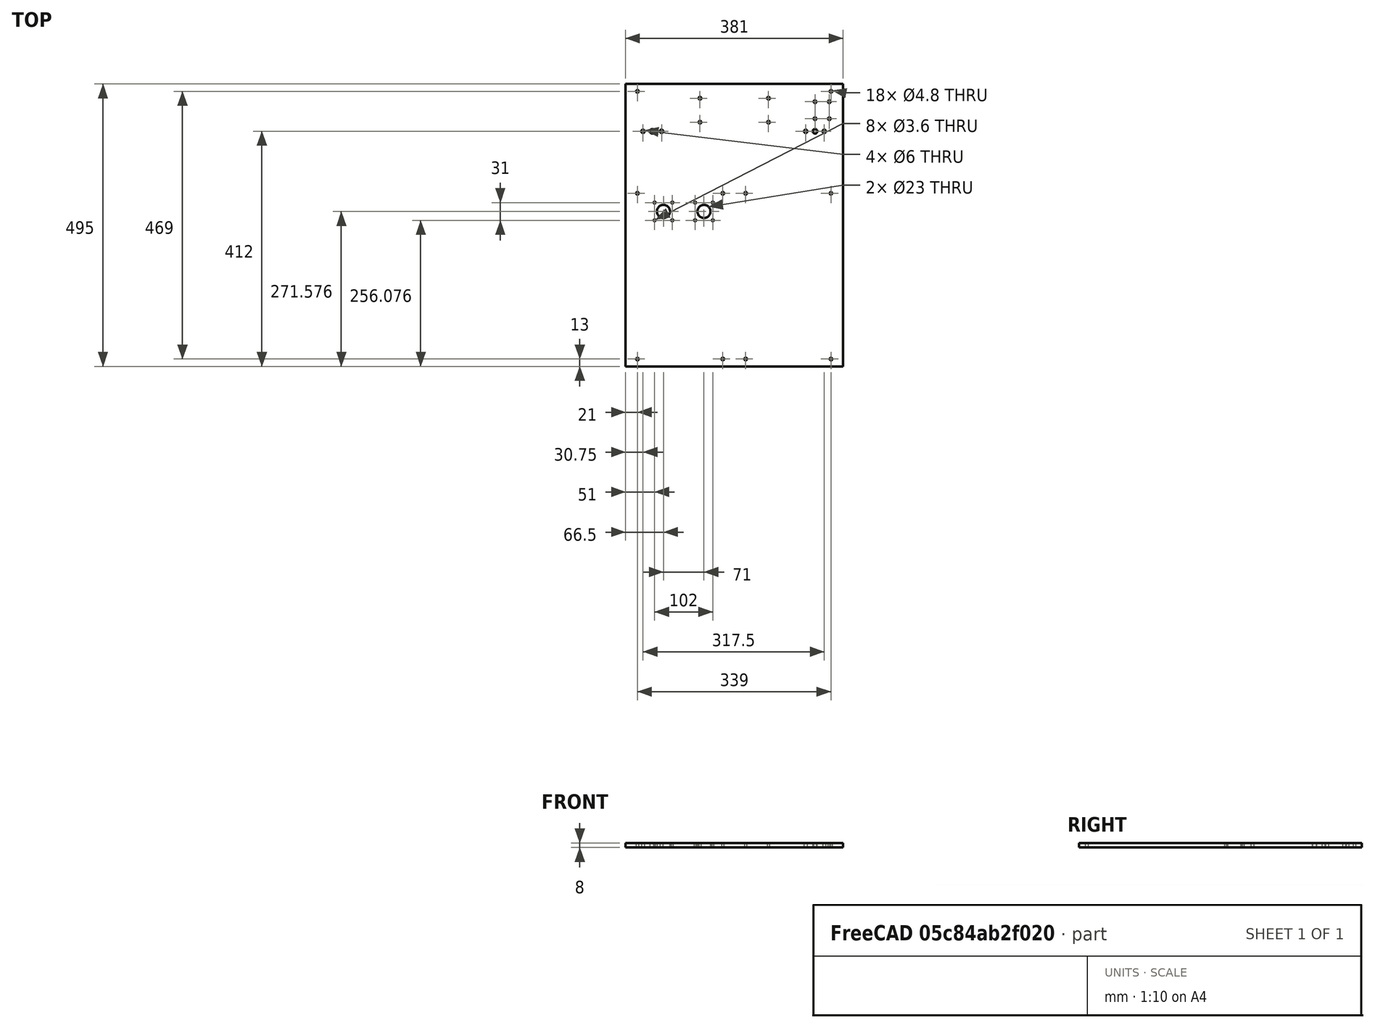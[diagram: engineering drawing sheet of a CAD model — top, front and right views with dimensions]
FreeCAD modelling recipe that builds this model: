
FCSTD DOCUMENT  (FreeCAD 0.16R6706 (Git))
Label: Fundo
License: All rights reserved
LicenseURL: http://en.wikipedia.org/wiki/All_rights_reserved
objects: Path::FeaturePython×37, Sketcher::SketchObject×1, PartDesign::Pad×1, Path::FeatureCompoundPython×1
note: 3 computed .brp shape members not serialized (recipe doc carries the construction recipe); baked Part::Feature solids carry a one-line shape summary decoded from their .brp

FEATURE [Sketcher::SketchObject] Sketch
  sketch-geometry (63):
    g0: LineSegment StartX=-381 StartY=495 StartZ=0 EndX=0 EndY=495 EndZ=0
    g1: LineSegment StartX=0 StartY=495 StartZ=0 EndX=0 EndY=0 EndZ=0
    g2: LineSegment StartX=-381 StartY=0 StartZ=0 EndX=-381 EndY=495 EndZ=0
    g3: LineSegment [constr] StartX=-334 StartY=400 StartZ=0 EndX=-334 EndY=412 EndZ=0
    g4: LineSegment [constr] StartX=-350.25 StartY=412 StartZ=0 EndX=-317.75 EndY=412 EndZ=0
    g5: Circle CenterX=-350.25 CenterY=412 CenterZ=0 NormalX=0 NormalY=0 NormalZ=1 Radius=3
    g6: Circle CenterX=-317.75 CenterY=412 CenterZ=0 NormalX=0 NormalY=0 NormalZ=1 Radius=3
    g7: Circle CenterX=-334 CenterY=412 CenterZ=0 NormalX=0 NormalY=0 NormalZ=1 Radius=4.05
    g8: LineSegment [constr] StartX=-334 StartY=412 StartZ=0 EndX=-49 EndY=412 EndZ=0
    g9: LineSegment [constr] StartX=-65.25 StartY=412 StartZ=0 EndX=-32.75 EndY=412 EndZ=0
    g10: Circle CenterX=-65.25 CenterY=412 CenterZ=0 NormalX=0 NormalY=0 NormalZ=1 Radius=3
    g11: Circle CenterX=-32.75 CenterY=412 CenterZ=0 NormalX=0 NormalY=0 NormalZ=1 Radius=3
    g12: Circle CenterX=-49 CenterY=412 CenterZ=0 NormalX=0 NormalY=0 NormalZ=1 Radius=4.05
    g13: LineSegment StartX=0 StartY=0 StartZ=0 EndX=-381 EndY=0 EndZ=0
    g14: Circle CenterX=-21 CenterY=482 CenterZ=0 NormalX=0 NormalY=0 NormalZ=1 Radius=2.4
    g15: LineSegment [constr] StartX=-360 StartY=482 StartZ=0 EndX=-21 EndY=482 EndZ=0
    g16: LineSegment [constr] StartX=-21 StartY=482 StartZ=0 EndX=-21 EndY=13 EndZ=0
    g17: LineSegment [constr] StartX=-21 StartY=13 StartZ=0 EndX=-360 EndY=13 EndZ=0
    g18: LineSegment [constr] StartX=-360 StartY=13 StartZ=0 EndX=-360 EndY=482 EndZ=0
    g19: Circle CenterX=-360 CenterY=482 CenterZ=0 NormalX=0 NormalY=0 NormalZ=1 Radius=2.4
    g20: Circle CenterX=-21 CenterY=13 CenterZ=0 NormalX=0 NormalY=0 NormalZ=1 Radius=2.4
    g21: Circle CenterX=-360 CenterY=13 CenterZ=0 NormalX=0 NormalY=0 NormalZ=1 Radius=2.4
    g22: LineSegment [constr] StartX=-250.5 StartY=470 StartZ=0 EndX=-250.5 EndY=428 EndZ=0
    g23: Circle CenterX=-250.5 CenterY=470 CenterZ=0 NormalX=0 NormalY=0 NormalZ=1 Radius=2.4
    g24: Circle CenterX=-250.5 CenterY=428 CenterZ=0 NormalX=0 NormalY=0 NormalZ=1 Radius=2.4
    g25: LineSegment [constr] StartX=-250.5 StartY=449 StartZ=0 EndX=-56.1898 EndY=449 EndZ=0
    g26: LineSegment [constr] StartX=-190.5 StartY=452.155 StartZ=0 EndX=-190.5 EndY=169.463 EndZ=0
    g27: LineSegment [constr] StartX=-210.5 StartY=303.4 StartZ=0 EndX=-170.5 EndY=303.4 EndZ=0
    g28: Circle CenterX=-210.5 CenterY=303.4 CenterZ=0 NormalX=0 NormalY=0 NormalZ=1 Radius=2.4
    g29: Circle CenterX=-170.5 CenterY=303.4 CenterZ=0 NormalX=0 NormalY=0 NormalZ=1 Radius=2.4
    g30: Circle CenterX=-360 CenterY=303.4 CenterZ=0 NormalX=0 NormalY=0 NormalZ=1 Radius=2.4
    g31: Circle CenterX=-21 CenterY=303.4 CenterZ=0 NormalX=0 NormalY=0 NormalZ=1 Radius=2.4
    g32: LineSegment [constr] StartX=-49 StartY=463.9 StartZ=0 EndX=-24 EndY=463.9 EndZ=0
    g33: LineSegment [constr] StartX=-24 StartY=463.9 StartZ=0 EndX=-24 EndY=434.1 EndZ=0
    g34: LineSegment [constr] StartX=-24 StartY=434.1 StartZ=0 EndX=-49 EndY=434.1 EndZ=0
    g35: LineSegment [constr] StartX=-49 StartY=434.1 StartZ=0 EndX=-49 EndY=463.9 EndZ=0
    g36: Circle CenterX=-49 CenterY=463.9 CenterZ=0 NormalX=0 NormalY=0 NormalZ=1 Radius=2.4
    g37: Circle CenterX=-24 CenterY=463.9 CenterZ=0 NormalX=0 NormalY=0 NormalZ=1 Radius=2.4
    g38: Circle CenterX=-24 CenterY=434.1 CenterZ=0 NormalX=0 NormalY=0 NormalZ=1 Radius=2.4
    g39: Circle CenterX=-49 CenterY=434.1 CenterZ=0 NormalX=0 NormalY=0 NormalZ=1 Radius=2.4
    g40: Circle CenterX=-210.5 CenterY=13 CenterZ=0 NormalX=0 NormalY=0 NormalZ=1 Radius=2.4
    g41: Circle CenterX=-170.5 CenterY=13 CenterZ=0 NormalX=0 NormalY=0 NormalZ=1 Radius=2.4
    g42: LineSegment [constr] StartX=-330 StartY=287.076 StartZ=0 EndX=-299 EndY=287.076 EndZ=0
    g43: LineSegment [constr] StartX=-299 StartY=287.076 StartZ=0 EndX=-299 EndY=256.076 EndZ=0
    g44: LineSegment [constr] StartX=-299 StartY=256.076 StartZ=0 EndX=-330 EndY=256.076 EndZ=0
    g45: LineSegment [constr] StartX=-330 StartY=256.076 StartZ=0 EndX=-330 EndY=287.076 EndZ=0
    g46: Circle CenterX=-314.5 CenterY=271.576 CenterZ=0 NormalX=0 NormalY=0 NormalZ=1 Radius=11.5
    g47: Circle CenterX=-330 CenterY=287.076 CenterZ=0 NormalX=0 NormalY=0 NormalZ=1 Radius=1.8
    g48: Circle CenterX=-299 CenterY=287.076 CenterZ=0 NormalX=0 NormalY=0 NormalZ=1 Radius=1.8
    g49: Circle CenterX=-299 CenterY=256.076 CenterZ=0 NormalX=0 NormalY=0 NormalZ=1 Radius=1.8
    g50: Circle CenterX=-330 CenterY=256.076 CenterZ=0 NormalX=0 NormalY=0 NormalZ=1 Radius=1.8
    g51: LineSegment [constr] StartX=-259 StartY=287.076 StartZ=0 EndX=-228 EndY=287.076 EndZ=0
    g52: LineSegment [constr] StartX=-228 StartY=287.076 StartZ=0 EndX=-228 EndY=256.076 EndZ=0
    g53: LineSegment [constr] StartX=-228 StartY=256.076 StartZ=0 EndX=-259 EndY=256.076 EndZ=0
    g54: LineSegment [constr] StartX=-259 StartY=256.076 StartZ=0 EndX=-259 EndY=287.076 EndZ=0
    g55: Circle CenterX=-243.5 CenterY=271.576 CenterZ=0 NormalX=0 NormalY=0 NormalZ=1 Radius=11.5
    g56: Circle CenterX=-259 CenterY=287.076 CenterZ=0 NormalX=0 NormalY=0 NormalZ=1 Radius=1.8
    g57: Circle CenterX=-228 CenterY=287.076 CenterZ=0 NormalX=0 NormalY=0 NormalZ=1 Radius=1.8
    g58: Circle CenterX=-228 CenterY=256.076 CenterZ=0 NormalX=0 NormalY=0 NormalZ=1 Radius=1.8
    g59: Circle CenterX=-259 CenterY=256.076 CenterZ=0 NormalX=0 NormalY=0 NormalZ=1 Radius=1.8
    g60: LineSegment [constr] StartX=-130.5 StartY=470 StartZ=0 EndX=-130.5 EndY=428 EndZ=0
    g61: Circle CenterX=-130.5 CenterY=470 CenterZ=0 NormalX=0 NormalY=0 NormalZ=1 Radius=2.4
    g62: Circle CenterX=-130.5 CenterY=428 CenterZ=0 NormalX=0 NormalY=0 NormalZ=1 Radius=2.4
  constraints (159):
    c: Coincident(g0,g1)
    c: Coincident(g2,g0)
    c: Horizontal(g0)
    c: Vertical(g1)
    c: Vertical(g2)
    c: DistanceY(g1,g1) = 495
    c: Vertical(g3)
    c: Horizontal(g4)
    c: DistanceX(g4,g4) = 32.5
    c: Radius(g5) = 3
    c: Equal(g5,g6) = 3
    c: Coincident(g4,g6)
    c: Coincident(g5,g4)
    c: Radius(g7) = 4.05
    c: Symmetric(g4,g4,g7)
    c: Coincident(g3,g7)
    c: Horizontal(g8)
    c: DistanceX(g8,g8) = 285
    c: Coincident(g3,g8)
    c: Horizontal(g9)
    c: Equal(g4,g9) = 32.5
    c: Equal(g5,g10) = 3
    c: Equal(g10,g11) = 3
    c: Coincident(g9,g11)
    c: Coincident(g10,g9)
    c: Equal(g7,g12) = 4.2
    c: Symmetric(g9,g9,g12)
    c: Coincident(g2,g13)
    c: Coincident(g1,g13)
    c: Horizontal(g13)
    c: Coincident(g12,g8)
    c: PointOnObject(g2,g-1)
    c: Coincident(g1,g-1)
    c: Radius(g14) = 2.4
    c: Coincident(g15,g16)
    c: Coincident(g16,g17)
    c: Coincident(g17,g18)
    c: Coincident(g18,g15)
    c: Horizontal(g15)
    c: Horizontal(g17)
    c: Vertical(g16)
    c: Vertical(g18)
    c: Coincident(g15,g14)
    c: DistanceX(g14,g0) = 21
    c: DistanceX(g15,g15) = 339
    c: DistanceX(g13,g13) = 381
    c: Equal(g14,g19) = 2.25
    c: Coincident(g15,g19)
    c: DistanceY(g14,g0) = 13
    c: DistanceX(g0,g15) = 21
    c: DistanceX(g8,g0) = 49
    c: DistanceX(g0,g3) = 47
    c: DistanceY(g2,g17) = 13
    c: Equal(g14,g20) = 2.25
    c: Equal(g14,g21) = 2.25
    c: Coincident(g17,g21)
    c: Coincident(g16,g20)
    c: Vertical(g22)
    c: Coincident(g22,g23)
    c: Coincident(g22,g24)
    c: DistanceY(g25,g14) = 33
    c: DistanceY(g22,g22) = 42
    c: Symmetric(g22,g22,g25)
    c: DistanceY(g8,g25) = 37
    c: Symmetric(g0,g0,g26)
    c: DistanceX(g25,g26) = 60
    c: Radius(g23) = 2.4
    c: Equal(g23,g24)
    c: Horizontal(g27)
    c: DistanceX(g27,g27) = 40
    c: Symmetric(g27,g27,g26)
    c: DistanceY(g27,g0) = 191.6
    c: Radius(g28) = 2.4
    c: Equal(g28,g29) = 2.4
    c: Coincident(g27,g29)
    c: Coincident(g27,g28)
    c: Equal(g28,g30) = 2.4
    c: Equal(g28,g31) = 2.4
    c: PointOnObject(g31,g27)
    c: PointOnObject(g30,g27)
    c: PointOnObject(g30,g18)
    c: PointOnObject(g31,g16)
    c: Coincident(g32,g33)
    c: Coincident(g33,g34)
    c: Coincident(g34,g35)
    c: Coincident(g35,g32)
    c: Horizontal(g32)
    c: Horizontal(g34)
    c: Vertical(g33)
    c: Vertical(g35)
    c: DistanceY(g35,g35) = 29.8
    c: DistanceX(g32,g32) = 25
    c: Symmetric(g32,g34,g25)
    c: DistanceX(g32,g0) = 49
    c: Radius(g36) = 2.4
    c: Equal(g36,g37) = 2.4
    c: Equal(g36,g38) = 2.4
    c: Equal(g36,g39) = 2.4
    c: Coincident(g32,g36)
    c: Coincident(g32,g37)
    c: Coincident(g33,g38)
    c: Coincident(g34,g39)
    c: Radius(g40) = 2.4
    c: Equal(g40,g41) = 2.4
    c: DistanceX(g40,g41) = 40
    c: PointOnObject(g40,g17)
    c: PointOnObject(g41,g17)
    c: DistanceX(g17,g40) = 149.5
    c: Coincident(g42,g43)
    c: Coincident(g43,g44)
    c: Coincident(g44,g45)
    c: Coincident(g45,g42)
    c: Horizontal(g42)
    c: Horizontal(g44)
    c: Vertical(g43)
    c: Vertical(g45)
    c: DistanceX(g42,g42) = 31
    c: Equal(g42,g45)
    c: Radius(g46) = 11.5
    c: Symmetric(g42,g44,g46)
    c: Radius(g47) = 1.8
    c: Equal(g47,g48) = 1.8
    c: Equal(g47,g49) = 1.8
    c: Equal(g47,g50) = 1.8
    c: Coincident(g47,g42)
    c: Coincident(g48,g42)
    c: Coincident(g43,g49)
    c: Coincident(g44,g50)
    c: Coincident(g51,g52)
    c: Coincident(g52,g53)
    c: Coincident(g53,g54)
    c: Coincident(g54,g51)
    c: Horizontal(g51)
    c: Horizontal(g53)
    c: Vertical(g52)
    c: Vertical(g54)
    c: Equal(g42,g51) = 31
    c: Equal(g51,g54)
    c: Equal(g46,g55) = 11.5
    c: Symmetric(g51,g53,g55)
    c: Equal(g47,g56) = 1.8
    c: Equal(g56,g57) = 1.8
    c: Equal(g56,g58) = 1.8
    c: Equal(g56,g59) = 1.8
    c: Coincident(g56,g51)
    c: Coincident(g57,g51)
    c: Coincident(g52,g58)
    c: Coincident(g53,g59)
    c: PointOnObject(g51,g42)
    c: DistanceX(g42,g51) = 40
    c: DistanceX(g30,g42) = 30
    c: Equal(g22,g60)
    c: Vertical(g60)
    c: Symmetric(g60,g60,g25)
    c: Equal(g23,g61) = 2.4
    c: Equal(g23,g62) = 2.4
    c: Coincident(g60,g62)
    c: Coincident(g61,g60)
    c: DistanceX(g26,g60) = 60
FEATURE [PartDesign::Pad] Pad
  Length = 8
  Length2 = 100
  Sketch = -> Sketch
  Type = 0
FEATURE [Path::FeaturePython] Machine  label="Machine_"  # Path/CAM operation (typed FeaturePython)
  MachineUnits = 0
  X = 0
  X_Max = 0
  X_Min = 0
  Y = 0
  Y_Max = 0
  Y_Min = 0
  Z = 0
  Z_Max = 0
  Z_Min = 0
FEATURE [Path::FeaturePython] Tool  label="Tool1"  # Path/CAM operation (typed FeaturePython)
  SpindleDir = 0
  SpindleSpeed = 0
  ToolNumber = 1
FEATURE [Path::FeaturePython] Profile  label="Cantoneiras"  # Path/CAM operation (typed FeaturePython)
  Active = true
  Base = -> Pad
  ClearanceHeight = 3.1
  Direction = 1
  Edge1 = -> Pad [Edge39]
  EndPoint = (0,0,0)
  ExtendAtEnd = 0
  ExtendAtStart = 0
  FinalDepth = -8.15
  HorizFeed = 127
  LeadInLineLen = 0
  LeadOutLineLen = 0
  OffsetExtra = 0
  PathClosed = true
  RetractHeight = 0
  RollRadius = 0
  SegLen = 0.5
  Side = 1
  StartDepth = 0
  StartPoint = (0,0,0)
  StepDown = 3
  ToolNumber = 1
  UseEndPoint = false
  UsePlacements = false
  UseStartDepth = true
  UseStartPoint = false
  VertFeed = 127
FEATURE [Path::FeaturePython] Profile001  label="Cantoneiras001"  # Path/CAM operation (typed FeaturePython)
  Active = true
  Base = -> Pad
  ClearanceHeight = 3.1
  Direction = 1
  Edge1 = -> Pad [Edge51]
  EndPoint = (0,0,0)
  ExtendAtEnd = 0
  ExtendAtStart = 0
  FinalDepth = -8.15
  HorizFeed = 127
  LeadInLineLen = 0
  LeadOutLineLen = 0
  OffsetExtra = 0
  PathClosed = true
  RetractHeight = 0
  RollRadius = 0
  SegLen = 0.5
  Side = 1
  StartDepth = 0
  StartPoint = (0,0,0)
  StepDown = 3
  ToolNumber = 1
  UseEndPoint = false
  UsePlacements = false
  UseStartDepth = true
  UseStartPoint = false
  VertFeed = 127
FEATURE [Path::FeaturePython] Profile002  label="Cantoneiras002"  # Path/CAM operation (typed FeaturePython)
  Active = true
  Base = -> Pad
  ClearanceHeight = 3.1
  Direction = 1
  Edge1 = -> Pad [Edge48]
  EndPoint = (0,0,0)
  ExtendAtEnd = 0
  ExtendAtStart = 0
  FinalDepth = -8.15
  HorizFeed = 127
  LeadInLineLen = 0
  LeadOutLineLen = 0
  OffsetExtra = 0
  PathClosed = true
  RetractHeight = 0
  RollRadius = 0
  SegLen = 0.5
  Side = 1
  StartDepth = 0
  StartPoint = (0,0,0)
  StepDown = 3
  ToolNumber = 1
  UseEndPoint = false
  UsePlacements = false
  UseStartDepth = true
  UseStartPoint = false
  VertFeed = 127
FEATURE [Path::FeaturePython] Profile003  label="Cantoneiras003"  # Path/CAM operation (typed FeaturePython)
  Active = true
  Base = -> Pad
  ClearanceHeight = 3.1
  Direction = 1
  Edge1 = -> Pad [Edge69]
  EndPoint = (0,0,0)
  ExtendAtEnd = 0
  ExtendAtStart = 0
  FinalDepth = -8.15
  HorizFeed = 127
  LeadInLineLen = 0
  LeadOutLineLen = 0
  OffsetExtra = 0
  PathClosed = true
  RetractHeight = 0
  RollRadius = 0
  SegLen = 0.5
  Side = 1
  StartDepth = 0
  StartPoint = (0,0,0)
  StepDown = 3
  ToolNumber = 1
  UseEndPoint = false
  UsePlacements = false
  UseStartDepth = true
  UseStartPoint = false
  VertFeed = 127
FEATURE [Path::FeaturePython] Profile004  label="Cantoneiras004"  # Path/CAM operation (typed FeaturePython)
  Active = true
  Base = -> Pad
  ClearanceHeight = 3.1
  Direction = 1
  Edge1 = -> Pad [Edge72]
  EndPoint = (0,0,0)
  ExtendAtEnd = 0
  ExtendAtStart = 0
  FinalDepth = -8.15
  HorizFeed = 127
  LeadInLineLen = 0
  LeadOutLineLen = 0
  OffsetExtra = 0
  PathClosed = true
  RetractHeight = 0
  RollRadius = 0
  SegLen = 0.5
  Side = 1
  StartDepth = 0
  StartPoint = (0,0,0)
  StepDown = 3
  ToolNumber = 1
  UseEndPoint = false
  UsePlacements = false
  UseStartDepth = true
  UseStartPoint = false
  VertFeed = 127
FEATURE [Path::FeaturePython] Profile005  label="Cantoneiras005"  # Path/CAM operation (typed FeaturePython)
  Active = true
  Base = -> Pad
  ClearanceHeight = 3.1
  Direction = 1
  Edge1 = -> Pad [Edge42]
  EndPoint = (0,0,0)
  ExtendAtEnd = 0
  ExtendAtStart = 0
  FinalDepth = -8.15
  HorizFeed = 127
  LeadInLineLen = 0
  LeadOutLineLen = 0
  OffsetExtra = 0
  PathClosed = true
  RetractHeight = 0
  RollRadius = 0
  SegLen = 0.5
  Side = 1
  StartDepth = 0
  StartPoint = (0,0,0)
  StepDown = 3
  ToolNumber = 1
  UseEndPoint = false
  UsePlacements = false
  UseStartDepth = true
  UseStartPoint = false
  VertFeed = 127
FEATURE [Path::FeaturePython] Profile006  label="Cantoneiras006"  # Path/CAM operation (typed FeaturePython)
  Active = true
  Base = -> Pad
  ClearanceHeight = 3.1
  Direction = 1
  Edge1 = -> Pad [Edge63]
  EndPoint = (0,0,0)
  ExtendAtEnd = 0
  ExtendAtStart = 0
  FinalDepth = -8.15
  HorizFeed = 127
  LeadInLineLen = 0
  LeadOutLineLen = 0
  OffsetExtra = 0
  PathClosed = true
  RetractHeight = 0
  RollRadius = 0
  SegLen = 0.5
  Side = 1
  StartDepth = 0
  StartPoint = (0,0,0)
  StepDown = 3
  ToolNumber = 1
  UseEndPoint = false
  UsePlacements = false
  UseStartDepth = true
  UseStartPoint = false
  VertFeed = 127
FEATURE [Path::FeaturePython] Profile007  label="Cantoneiras007"  # Path/CAM operation (typed FeaturePython)
  Active = true
  Base = -> Pad
  ClearanceHeight = 3.1
  Direction = 1
  Edge1 = -> Pad [Edge90]
  EndPoint = (0,0,0)
  ExtendAtEnd = 0
  ExtendAtStart = 0
  FinalDepth = -8.15
  HorizFeed = 127
  LeadInLineLen = 0
  LeadOutLineLen = 0
  OffsetExtra = 0
  PathClosed = true
  RetractHeight = 0
  RollRadius = 0
  SegLen = 0.5
  Side = 1
  StartDepth = 0
  StartPoint = (0,0,0)
  StepDown = 3
  ToolNumber = 1
  UseEndPoint = false
  UsePlacements = false
  UseStartDepth = true
  UseStartPoint = false
  VertFeed = 127
FEATURE [Path::FeaturePython] Profile008  label="Cantoneiras008"  # Path/CAM operation (typed FeaturePython)
  Active = true
  Base = -> Pad
  ClearanceHeight = 3.1
  Direction = 1
  Edge1 = -> Pad [Edge87]
  EndPoint = (0,0,0)
  ExtendAtEnd = 0
  ExtendAtStart = 0
  FinalDepth = -8.15
  HorizFeed = 127
  LeadInLineLen = 0
  LeadOutLineLen = 0
  OffsetExtra = 0
  PathClosed = true
  RetractHeight = 0
  RollRadius = 0
  SegLen = 0.5
  Side = 1
  StartDepth = 0
  StartPoint = (0,0,0)
  StepDown = 3
  ToolNumber = 1
  UseEndPoint = false
  UsePlacements = false
  UseStartDepth = true
  UseStartPoint = false
  VertFeed = 127
FEATURE [Path::FeaturePython] Profile009  label="Cantoneiras009"  # Path/CAM operation (typed FeaturePython)
  Active = true
  Base = -> Pad
  ClearanceHeight = 3.1
  Direction = 1
  Edge1 = -> Pad [Edge84]
  EndPoint = (0,0,0)
  ExtendAtEnd = 0
  ExtendAtStart = 0
  FinalDepth = -8.15
  HorizFeed = 127
  LeadInLineLen = 0
  LeadOutLineLen = 0
  OffsetExtra = 0
  PathClosed = true
  RetractHeight = 0
  RollRadius = 0
  SegLen = 0.5
  Side = 1
  StartDepth = 0
  StartPoint = (0,0,0)
  StepDown = 3
  ToolNumber = 1
  UseEndPoint = false
  UsePlacements = false
  UseStartDepth = true
  UseStartPoint = false
  VertFeed = 127
FEATURE [Path::FeaturePython] Profile010  label="Motores"  # Path/CAM operation (typed FeaturePython)
  Active = true
  Base = -> Pad
  ClearanceHeight = 3.1
  Direction = 1
  Edge1 = -> Pad [Edge93]
  EndPoint = (0,0,0)
  ExtendAtEnd = 0
  ExtendAtStart = 0
  FinalDepth = -8.15
  HorizFeed = 127
  LeadInLineLen = 0
  LeadOutLineLen = 0
  OffsetExtra = 0
  PathClosed = true
  RetractHeight = 0
  RollRadius = 0
  SegLen = 0.5
  Side = 1
  StartDepth = 0
  StartPoint = (0,0,0)
  StepDown = 3
  ToolNumber = 1
  UseEndPoint = false
  UsePlacements = false
  UseStartDepth = true
  UseStartPoint = false
  VertFeed = 127
FEATURE [Path::FeaturePython] Profile011  label="Motores001"  # Path/CAM operation (typed FeaturePython)
  Active = true
  Base = -> Pad
  ClearanceHeight = 3.1
  Direction = 1
  Edge1 = -> Pad [Edge96]
  EndPoint = (0,0,0)
  ExtendAtEnd = 0
  ExtendAtStart = 0
  FinalDepth = -8.15
  HorizFeed = 127
  LeadInLineLen = 0
  LeadOutLineLen = 0
  OffsetExtra = 0
  PathClosed = true
  RetractHeight = 0
  RollRadius = 0
  SegLen = 0.5
  Side = 1
  StartDepth = 0
  StartPoint = (0,0,0)
  StepDown = 3
  ToolNumber = 1
  UseEndPoint = false
  UsePlacements = false
  UseStartDepth = true
  UseStartPoint = false
  VertFeed = 127
FEATURE [Path::FeaturePython] Profile012  label="Motores002"  # Path/CAM operation (typed FeaturePython)
  Active = true
  Base = -> Pad
  ClearanceHeight = 3.1
  Direction = 1
  Edge1 = -> Pad [Edge18]
  EndPoint = (0,0,0)
  ExtendAtEnd = 0
  ExtendAtStart = 0
  FinalDepth = -8.15
  HorizFeed = 127
  LeadInLineLen = 0
  LeadOutLineLen = 0
  OffsetExtra = 0
  PathClosed = true
  RetractHeight = 0
  RollRadius = 0
  SegLen = 0.5
  Side = 1
  StartDepth = 0
  StartPoint = (0,0,0)
  StepDown = 3
  ToolNumber = 1
  UseEndPoint = false
  UsePlacements = false
  UseStartDepth = true
  UseStartPoint = false
  VertFeed = 127
FEATURE [Path::FeaturePython] Profile013  label="Motores003"  # Path/CAM operation (typed FeaturePython)
  Active = true
  Base = -> Pad
  ClearanceHeight = 3.1
  Direction = 1
  Edge1 = -> Pad [Edge114]
  EndPoint = (0,0,0)
  ExtendAtEnd = 0
  ExtendAtStart = 0
  FinalDepth = -8.15
  HorizFeed = 127
  LeadInLineLen = 0
  LeadOutLineLen = 0
  OffsetExtra = 0
  PathClosed = true
  RetractHeight = 0
  RollRadius = 0
  SegLen = 0.5
  Side = 1
  StartDepth = 0
  StartPoint = (0,0,0)
  StepDown = 3
  ToolNumber = 1
  UseEndPoint = false
  UsePlacements = false
  UseStartDepth = true
  UseStartPoint = false
  VertFeed = 127
FEATURE [Path::FeaturePython] Profile014  label="Motores004"  # Path/CAM operation (typed FeaturePython)
  Active = true
  Base = -> Pad
  ClearanceHeight = 3.1
  Direction = 1
  Edge1 = -> Pad [Edge99]
  EndPoint = (0,0,0)
  ExtendAtEnd = 0
  ExtendAtStart = 0
  FinalDepth = -8.15
  HorizFeed = 127
  LeadInLineLen = 0
  LeadOutLineLen = 0
  OffsetExtra = 0
  PathClosed = true
  RetractHeight = 0
  RollRadius = 0
  SegLen = 0.5
  Side = 1
  StartDepth = 0
  StartPoint = (0,0,0)
  StepDown = 3
  ToolNumber = 1
  UseEndPoint = false
  UsePlacements = false
  UseStartDepth = true
  UseStartPoint = false
  VertFeed = 127
FEATURE [Path::FeaturePython] Profile015  label="Motores005"  # Path/CAM operation (typed FeaturePython)
  Active = true
  Base = -> Pad
  ClearanceHeight = 3.1
  Direction = 1
  Edge1 = -> Pad [Edge102]
  EndPoint = (0,0,0)
  ExtendAtEnd = 0
  ExtendAtStart = 0
  FinalDepth = -8.15
  HorizFeed = 127
  LeadInLineLen = 0
  LeadOutLineLen = 0
  OffsetExtra = 0
  PathClosed = true
  RetractHeight = 0
  RollRadius = 0
  SegLen = 0.5
  Side = 1
  StartDepth = 0
  StartPoint = (0,0,0)
  StepDown = 3
  ToolNumber = 1
  UseEndPoint = false
  UsePlacements = false
  UseStartDepth = true
  UseStartPoint = false
  VertFeed = 127
FEATURE [Path::FeaturePython] Profile016  label="Motores006"  # Path/CAM operation (typed FeaturePython)
  Active = true
  Base = -> Pad
  ClearanceHeight = 3.1
  Direction = 1
  Edge1 = -> Pad [Edge111]
  EndPoint = (0,0,0)
  ExtendAtEnd = 0
  ExtendAtStart = 0
  FinalDepth = -8.15
  HorizFeed = 127
  LeadInLineLen = 0
  LeadOutLineLen = 0
  OffsetExtra = 0
  PathClosed = true
  RetractHeight = 0
  RollRadius = 0
  SegLen = 0.5
  Side = 1
  StartDepth = 0
  StartPoint = (0,0,0)
  StepDown = 3
  ToolNumber = 1
  UseEndPoint = false
  UsePlacements = false
  UseStartDepth = true
  UseStartPoint = false
  VertFeed = 127
FEATURE [Path::FeaturePython] Profile017  label="Motores007"  # Path/CAM operation (typed FeaturePython)
  Active = true
  Base = -> Pad
  ClearanceHeight = 3.1
  Direction = 1
  Edge1 = -> Pad [Edge15]
  EndPoint = (0,0,0)
  ExtendAtEnd = 0
  ExtendAtStart = 0
  FinalDepth = -8.15
  HorizFeed = 127
  LeadInLineLen = 0
  LeadOutLineLen = 0
  OffsetExtra = 0
  PathClosed = true
  RetractHeight = 0
  RollRadius = 0
  SegLen = 0.5
  Side = 1
  StartDepth = 0
  StartPoint = (0,0,0)
  StepDown = 3
  ToolNumber = 1
  UseEndPoint = false
  UsePlacements = false
  UseStartDepth = true
  UseStartPoint = false
  VertFeed = 127
FEATURE [Path::FeaturePython] Profile018  label="Motores008"  # Path/CAM operation (typed FeaturePython)
  Active = true
  Base = -> Pad
  ClearanceHeight = 3.1
  Direction = 1
  Edge1 = -> Pad [Edge108]
  EndPoint = (0,0,0)
  ExtendAtEnd = 0
  ExtendAtStart = 0
  FinalDepth = -8.15
  HorizFeed = 127
  LeadInLineLen = 0
  LeadOutLineLen = 0
  OffsetExtra = 0
  PathClosed = true
  RetractHeight = 0
  RollRadius = 0
  SegLen = 0.5
  Side = 1
  StartDepth = 0
  StartPoint = (0,0,0)
  StepDown = 3
  ToolNumber = 1
  UseEndPoint = false
  UsePlacements = false
  UseStartDepth = true
  UseStartPoint = false
  VertFeed = 127
FEATURE [Path::FeaturePython] Profile019  label="Motores009"  # Path/CAM operation (typed FeaturePython)
  Active = true
  Base = -> Pad
  ClearanceHeight = 3.1
  Direction = 1
  Edge1 = -> Pad [Edge105]
  EndPoint = (0,0,0)
  ExtendAtEnd = 0
  ExtendAtStart = 0
  FinalDepth = -8.15
  HorizFeed = 127
  LeadInLineLen = 0
  LeadOutLineLen = 0
  OffsetExtra = 0
  PathClosed = true
  RetractHeight = 0
  RollRadius = 0
  SegLen = 0.5
  Side = 1
  StartDepth = 0
  StartPoint = (0,0,0)
  StepDown = 3
  ToolNumber = 1
  UseEndPoint = false
  UsePlacements = false
  UseStartDepth = true
  UseStartPoint = false
  VertFeed = 127
FEATURE [Path::FeaturePython] Profile020  label="Eixos"  # Path/CAM operation (typed FeaturePython)
  Active = true
  Base = -> Pad
  ClearanceHeight = 3.1
  Direction = 1
  Edge1 = -> Pad [Edge27]
  EndPoint = (0,0,0)
  ExtendAtEnd = 0
  ExtendAtStart = 0
  FinalDepth = -8.15
  HorizFeed = 127
  LeadInLineLen = 0
  LeadOutLineLen = 0
  OffsetExtra = 0
  PathClosed = true
  RetractHeight = 0
  RollRadius = 0
  SegLen = 0.5
  Side = 1
  StartDepth = 0
  StartPoint = (0,0,0)
  StepDown = 3
  ToolNumber = 1
  UseEndPoint = false
  UsePlacements = false
  UseStartDepth = true
  UseStartPoint = false
  VertFeed = 127
FEATURE [Path::FeaturePython] Profile021  label="Eixos001"  # Path/CAM operation (typed FeaturePython)
  Active = true
  Base = -> Pad
  ClearanceHeight = 3.1
  Direction = 1
  Edge1 = -> Pad [Edge21]
  EndPoint = (0,0,0)
  ExtendAtEnd = 0
  ExtendAtStart = 0
  FinalDepth = -8.15
  HorizFeed = 127
  LeadInLineLen = 0
  LeadOutLineLen = 0
  OffsetExtra = 0
  PathClosed = true
  RetractHeight = 0
  RollRadius = 0
  SegLen = 0.5
  Side = 1
  StartDepth = 0
  StartPoint = (0,0,0)
  StepDown = 3
  ToolNumber = 1
  UseEndPoint = false
  UsePlacements = false
  UseStartDepth = true
  UseStartPoint = false
  VertFeed = 127
FEATURE [Path::FeaturePython] Profile022  label="Eixos002"  # Path/CAM operation (typed FeaturePython)
  Active = true
  Base = -> Pad
  ClearanceHeight = 3.1
  Direction = 1
  Edge1 = -> Pad [Edge30]
  EndPoint = (0,0,0)
  ExtendAtEnd = 0
  ExtendAtStart = 0
  FinalDepth = -8.15
  HorizFeed = 127
  LeadInLineLen = 0
  LeadOutLineLen = 0
  OffsetExtra = 0
  PathClosed = true
  RetractHeight = 0
  RollRadius = 0
  SegLen = 0.5
  Side = 1
  StartDepth = 0
  StartPoint = (0,0,0)
  StepDown = 3
  ToolNumber = 1
  UseEndPoint = false
  UsePlacements = false
  UseStartDepth = true
  UseStartPoint = false
  VertFeed = 127
FEATURE [Path::FeaturePython] Profile023  label="Eixos003"  # Path/CAM operation (typed FeaturePython)
  Active = true
  Base = -> Pad
  ClearanceHeight = 3.1
  Direction = 1
  Edge1 = -> Pad [Edge33]
  EndPoint = (0,0,0)
  ExtendAtEnd = 0
  ExtendAtStart = 0
  FinalDepth = -8.15
  HorizFeed = 127
  LeadInLineLen = 0
  LeadOutLineLen = 0
  OffsetExtra = 0
  PathClosed = true
  RetractHeight = 0
  RollRadius = 0
  SegLen = 0.5
  Side = 1
  StartDepth = 0
  StartPoint = (0,0,0)
  StepDown = 3
  ToolNumber = 1
  UseEndPoint = false
  UsePlacements = false
  UseStartDepth = true
  UseStartPoint = false
  VertFeed = 127
FEATURE [Path::FeaturePython] Profile024  label="Eixos004"  # Path/CAM operation (typed FeaturePython)
  Active = true
  Base = -> Pad
  ClearanceHeight = 3.1
  Direction = 1
  Edge1 = -> Pad [Edge24]
  EndPoint = (0,0,0)
  ExtendAtEnd = 0
  ExtendAtStart = 0
  FinalDepth = -8.15
  HorizFeed = 127
  LeadInLineLen = 0
  LeadOutLineLen = 0
  OffsetExtra = 0
  PathClosed = true
  RetractHeight = 0
  RollRadius = 0
  SegLen = 0.5
  Side = 1
  StartDepth = 0
  StartPoint = (0,0,0)
  StepDown = 3
  ToolNumber = 1
  UseEndPoint = false
  UsePlacements = false
  UseStartDepth = true
  UseStartPoint = false
  VertFeed = 127
FEATURE [Path::FeaturePython] Profile025  label="Eixos005"  # Path/CAM operation (typed FeaturePython)
  Active = true
  Base = -> Pad
  ClearanceHeight = 3.1
  Direction = 1
  Edge1 = -> Pad [Edge36]
  EndPoint = (0,0,0)
  ExtendAtEnd = 0
  ExtendAtStart = 0
  FinalDepth = -8.15
  HorizFeed = 127
  LeadInLineLen = 0
  LeadOutLineLen = 0
  OffsetExtra = 0
  PathClosed = true
  RetractHeight = 0
  RollRadius = 0
  SegLen = 0.5
  Side = 1
  StartDepth = 0
  StartPoint = (0,0,0)
  StepDown = 3
  ToolNumber = 1
  UseEndPoint = false
  UsePlacements = false
  UseStartDepth = true
  UseStartPoint = false
  VertFeed = 127
FEATURE [Path::FeaturePython] Profile026  label="Suporte Motor"  # Path/CAM operation (typed FeaturePython)
  Active = true
  Base = -> Pad
  ClearanceHeight = 3.1
  Direction = 1
  Edge1 = -> Pad [Edge57]
  EndPoint = (0,0,0)
  ExtendAtEnd = 0
  ExtendAtStart = 0
  FinalDepth = -8.15
  HorizFeed = 127
  LeadInLineLen = 0
  LeadOutLineLen = 0
  OffsetExtra = 0
  PathClosed = true
  RetractHeight = 0
  RollRadius = 0
  SegLen = 0.5
  Side = 1
  StartDepth = 0
  StartPoint = (0,0,0)
  StepDown = 3
  ToolNumber = 1
  UseEndPoint = false
  UsePlacements = false
  UseStartDepth = true
  UseStartPoint = false
  VertFeed = 127
FEATURE [Path::FeaturePython] Profile027  label="Suporte Motor001"  # Path/CAM operation (typed FeaturePython)
  Active = true
  Base = -> Pad
  ClearanceHeight = 3.1
  Direction = 1
  Edge1 = -> Pad [Edge60]
  EndPoint = (0,0,0)
  ExtendAtEnd = 0
  ExtendAtStart = 0
  FinalDepth = -8.15
  HorizFeed = 127
  LeadInLineLen = 0
  LeadOutLineLen = 0
  OffsetExtra = 0
  PathClosed = true
  RetractHeight = 0
  RollRadius = 0
  SegLen = 0.5
  Side = 1
  StartDepth = 0
  StartPoint = (0,0,0)
  StepDown = 3
  ToolNumber = 1
  UseEndPoint = false
  UsePlacements = false
  UseStartDepth = true
  UseStartPoint = false
  VertFeed = 127
FEATURE [Path::FeaturePython] Profile028  label="Suporte Motor002"  # Path/CAM operation (typed FeaturePython)
  Active = true
  Base = -> Pad
  ClearanceHeight = 3.1
  Direction = 1
  Edge1 = -> Pad [Edge45]
  EndPoint = (0,0,0)
  ExtendAtEnd = 0
  ExtendAtStart = 0
  FinalDepth = -8.15
  HorizFeed = 127
  LeadInLineLen = 0
  LeadOutLineLen = 0
  OffsetExtra = 0
  PathClosed = true
  RetractHeight = 0
  RollRadius = 0
  SegLen = 0.5
  Side = 1
  StartDepth = 0
  StartPoint = (0,0,0)
  StepDown = 3
  ToolNumber = 1
  UseEndPoint = false
  UsePlacements = false
  UseStartDepth = true
  UseStartPoint = false
  VertFeed = 127
FEATURE [Path::FeaturePython] Profile029  label="Suporte Motor003"  # Path/CAM operation (typed FeaturePython)
  Active = true
  Base = -> Pad
  ClearanceHeight = 3.1
  Direction = 1
  Edge1 = -> Pad [Edge54]
  EndPoint = (0,0,0)
  ExtendAtEnd = 0
  ExtendAtStart = 0
  FinalDepth = -8.15
  HorizFeed = 127
  LeadInLineLen = 0
  LeadOutLineLen = 0
  OffsetExtra = 0
  PathClosed = true
  RetractHeight = 0
  RollRadius = 0
  SegLen = 0.5
  Side = 1
  StartDepth = 0
  StartPoint = (0,0,0)
  StepDown = 3
  ToolNumber = 1
  UseEndPoint = false
  UsePlacements = false
  UseStartDepth = true
  UseStartPoint = false
  VertFeed = 127
FEATURE [Path::FeaturePython] Profile030  label="Mancal"  # Path/CAM operation (typed FeaturePython)
  Active = true
  Base = -> Pad
  ClearanceHeight = 3.1
  Direction = 1
  Edge1 = -> Pad [Edge66]
  EndPoint = (0,0,0)
  ExtendAtEnd = 0
  ExtendAtStart = 0
  FinalDepth = -8.15
  HorizFeed = 127
  LeadInLineLen = 0
  LeadOutLineLen = 0
  OffsetExtra = 0
  PathClosed = true
  RetractHeight = 0
  RollRadius = 0
  SegLen = 0.5
  Side = 1
  StartDepth = 0
  StartPoint = (0,0,0)
  StepDown = 3
  ToolNumber = 1
  UseEndPoint = false
  UsePlacements = false
  UseStartDepth = true
  UseStartPoint = false
  VertFeed = 127
FEATURE [Path::FeaturePython] Profile031  label="Mancal001"  # Path/CAM operation (typed FeaturePython)
  Active = true
  Base = -> Pad
  ClearanceHeight = 3.1
  Direction = 1
  Edge1 = -> Pad [Edge81]
  EndPoint = (0,0,0)
  ExtendAtEnd = 0
  ExtendAtStart = 0
  FinalDepth = -8.15
  HorizFeed = 127
  LeadInLineLen = 0
  LeadOutLineLen = 0
  OffsetExtra = 0
  PathClosed = true
  RetractHeight = 0
  RollRadius = 0
  SegLen = 0.5
  Side = 1
  StartDepth = 0
  StartPoint = (0,0,0)
  StepDown = 3
  ToolNumber = 1
  UseEndPoint = false
  UsePlacements = false
  UseStartDepth = true
  UseStartPoint = false
  VertFeed = 127
FEATURE [Path::FeaturePython] Profile032  label="Mancal002"  # Path/CAM operation (typed FeaturePython)
  Active = true
  Base = -> Pad
  ClearanceHeight = 3.1
  Direction = 1
  Edge1 = -> Pad [Edge75]
  EndPoint = (0,0,0)
  ExtendAtEnd = 0
  ExtendAtStart = 0
  FinalDepth = -8.15
  HorizFeed = 127
  LeadInLineLen = 0
  LeadOutLineLen = 0
  OffsetExtra = 0
  PathClosed = true
  RetractHeight = 0
  RollRadius = 0
  SegLen = 0.5
  Side = 1
  StartDepth = 0
  StartPoint = (0,0,0)
  StepDown = 3
  ToolNumber = 1
  UseEndPoint = false
  UsePlacements = false
  UseStartDepth = true
  UseStartPoint = false
  VertFeed = 127
FEATURE [Path::FeaturePython] Profile033  label="Mancal003"  # Path/CAM operation (typed FeaturePython)
  Active = true
  Base = -> Pad
  ClearanceHeight = 3.1
  Direction = 1
  Edge1 = -> Pad [Edge78]
  EndPoint = (0,0,0)
  ExtendAtEnd = 0
  ExtendAtStart = 0
  FinalDepth = -8.15
  HorizFeed = 127
  LeadInLineLen = 0
  LeadOutLineLen = 0
  OffsetExtra = 0
  PathClosed = true
  RetractHeight = 0
  RollRadius = 0
  SegLen = 0.5
  Side = 1
  StartDepth = 0
  StartPoint = (0,0,0)
  StepDown = 3
  ToolNumber = 1
  UseEndPoint = false
  UsePlacements = false
  UseStartDepth = true
  UseStartPoint = false
  VertFeed = 127
FEATURE [Path::FeaturePython] Profile034  label="Externo"  # Path/CAM operation (typed FeaturePython)
  Active = true
  Base = -> Pad
  ClearanceHeight = 3.1
  Direction = 0
  EndPoint = (0,0,0)
  ExtendAtEnd = 0
  ExtendAtStart = 0
  Face1 = -> Pad [Face40]
  FinalDepth = -8.15
  HorizFeed = 127
  LeadInLineLen = 0
  LeadOutLineLen = 0
  OffsetExtra = 0
  PathClosed = true
  RetractHeight = 0
  RollRadius = 0
  SegLen = 0.5
  Side = 0
  StartDepth = 0
  StartPoint = (0,0,0)
  StepDown = 3
  ToolNumber = 1
  UseEndPoint = false
  UsePlacements = false
  UseStartDepth = true
  UseStartPoint = false
  VertFeed = 127
FEATURE [Path::FeatureCompoundPython] Project  # Path/CAM operation (typed FeaturePython)
  Group = -> [Machine,Tool,Profile,Profile001,Profile002,Profile003,Profile004,Profile005,Profile006,Profile007,Profile008,Profile009,Profile010,Profile011,Profile012,Profile013,Profile014,Profile015,Profile016,Profile017,Profile018,Profile019,Profile020,Profile021,Profile022,Profile023,Profile024,Profile025,Profile026,Profile027,Profile028,Profile029,Profile030,Profile031,Profile032,Profile033,Profile034]
  UsePlacements = false
